# Revit family: Hand_Shower_Holder-GROHE-Tempesta-27595001
name_source: partatom
category: Specialty Equipment
units: mm (PartAtom-declared; Revit-internal decimal feet)

## family parameters
Cut with Voids When Loaded = No
Host = Face
OmniClass Number = 23.45.05.14.17
OmniClass Title = Showers
Part Type = Normal
Room Calculation Point = No
Round Connector Dimension = Use Diameter
Shared = Yes

## types (1)
- 27595001
    Assembly Code = D2010710
    Default Elevation = 0 mm  [stored 0 ft]
    Description = TEMPESTA ADJUSTABLE HAND SHOWER HOLDER
    Finish = Metal-Grohe-001-StarLight Chrome
    Height = 50 mm  [stored 0.164042 ft]
    Installation Type = Wall Mounted
    Length = 84 mm  [stored 0.275591 ft]
    Manufacturer = Grohe
    Material = Metal-Grohe-001-StarLight Chrome
    Model = 27595001
    URL = https://www.grohe.com
    Width = 67 mm

note: [stored X ft] marks values corroborated as IEEE doubles in the binary element streams (Revit-internal decimal feet)

## geometry (parser evidence)
native form markers: Sweep x3
no freeform markers — native parametric forms only
